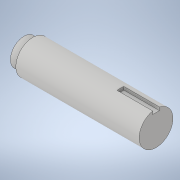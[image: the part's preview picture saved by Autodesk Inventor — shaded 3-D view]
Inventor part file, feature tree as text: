
AUTODESK INVENTOR PART (.ipt)
format: ipt  version: 2021 (Build 250183000, 183)  size: 116,224 bytes
history: native  units: in
note: dims shown in document units (in); Inventor stores cm internally (conversion verified against a paired STEP export)
features: extrude x3, sketch x3, plane x1
ambient origin geometry x8: Origin, YZ Plane, XZ Plane, XY Plane, X Axis, Y Axis, Z Axis, Center Point
bodies: Solid1 (feature_tree)
feature tree (7):
  extrude  "Extrusion1"  Depth=4.88in TaperAngle=0.0deg
  plane  "Work Plane1"
  extrude  "Extrusion9"  Depth=0.25in
  extrude  "Extrusion10"  Depth=1.313in TaperAngle=0.0deg
  sketch  "Sketch1"  dims[d0=1.25in d1=4.88in d2=0.0in]
  sketch  "Sketch9"  dims[d11=-2.0535in d26=0.25in]
  sketch  "Sketch10"  dims[d27=0.125in d28=1.313in d29=0.0in d30=1.0in d31=0.325in d32=0.0in]
